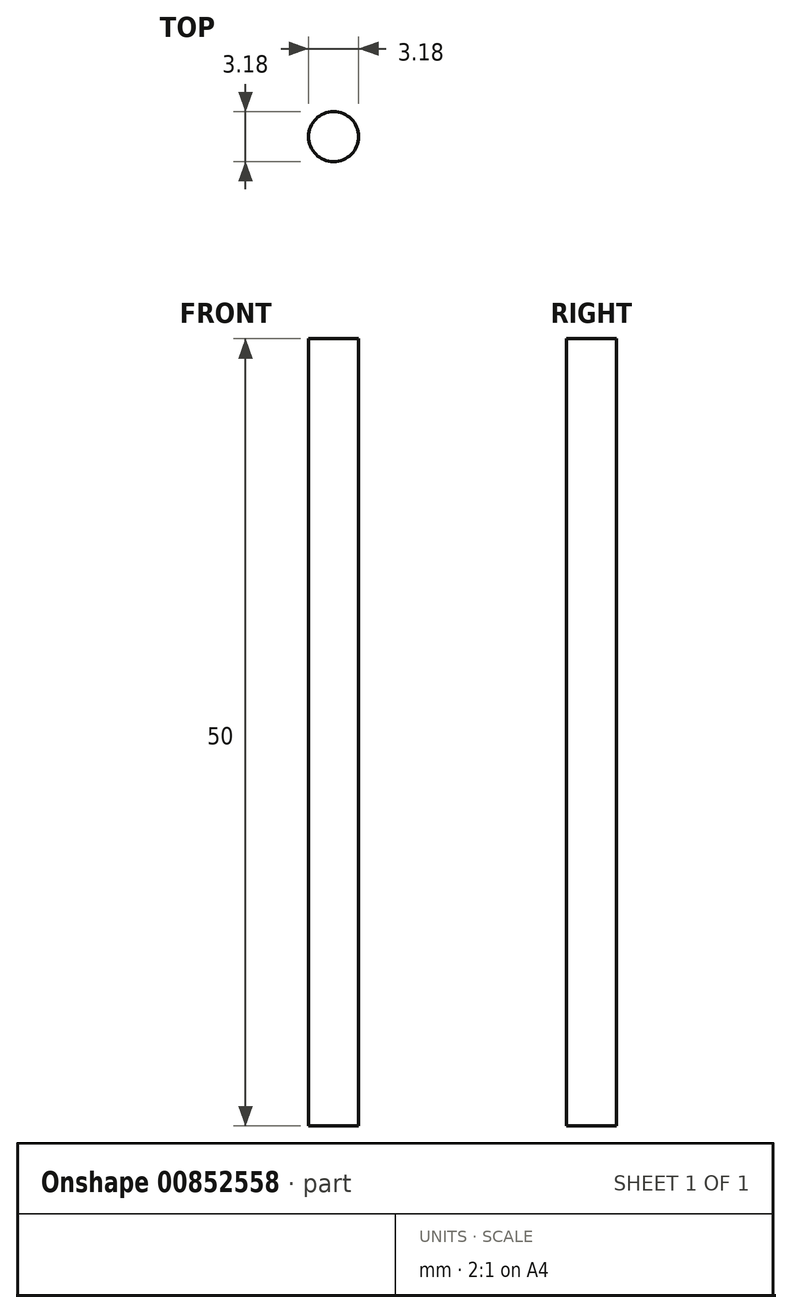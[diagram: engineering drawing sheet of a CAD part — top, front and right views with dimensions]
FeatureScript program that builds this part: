
annotation { "Feature Type Name" : "Feature", "Feature Type Description" : "" }
export const myFeature = defineFeature(function(context is Context, id is Id, definition is map)
    precondition{}
    {
        {
            var Q0;
            Q0=qCreatedBy(makeId("Top.planeOp"),FACE);
            var sketch = newSketch(context, id + "F0", { "sketchPlane" : qUnion([Q0])});
            skCircle(sketch, "E0", {"center": v(0, 0) * mm, "radius": 1.59 * mm});
            skSolve(sketch);
        }
        {
            var Q0;
            Q0=qSketchRegion(id+"F0",true);
            extrude(context, id + "F1", {"entities" : qUnion([Q0]), "depth" : 50 * mm, "offsetDistance" : 25 * mm});
        }
    });
